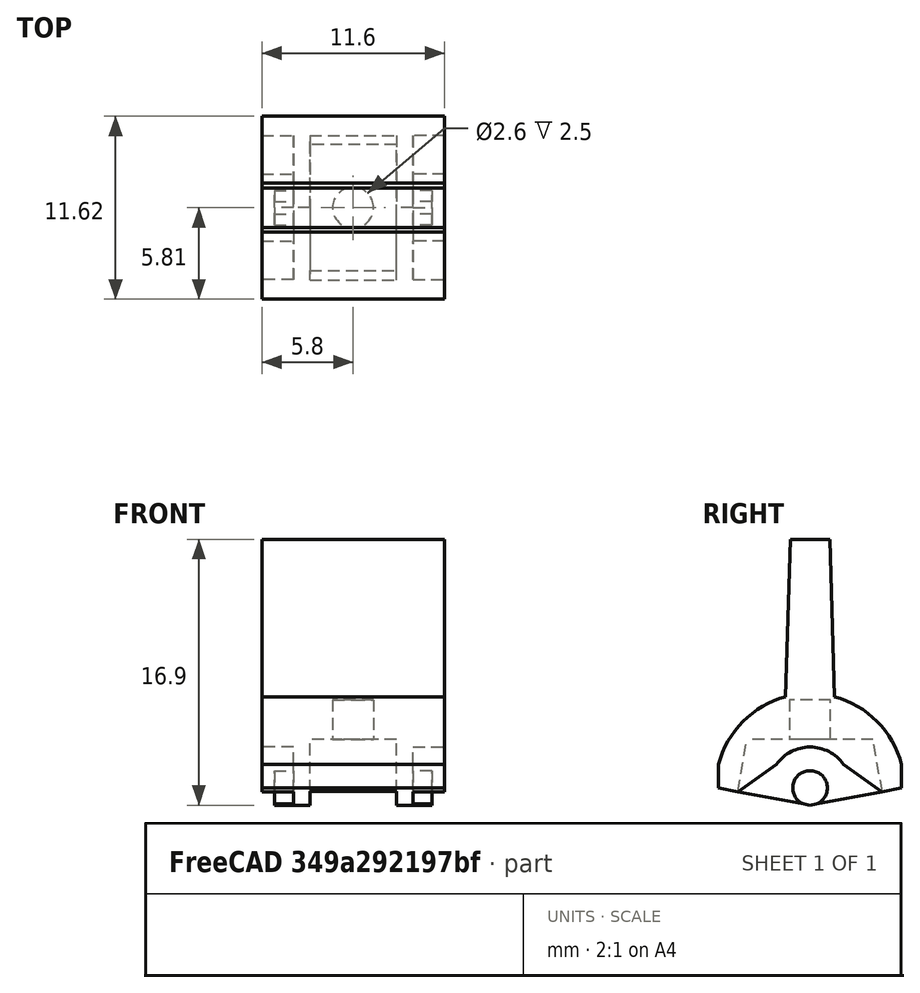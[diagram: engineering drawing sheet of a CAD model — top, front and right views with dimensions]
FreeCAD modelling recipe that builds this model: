
FCSTD DOCUMENT  (FreeCAD 1.0R39109 (Git))
Label: switch lever MA
License: All rights reserved
LicenseURL: http://en.wikipedia.org/wiki/All_rights_reserved
objects: Sketcher::SketchObject×6, PartDesign::Pocket×4, PartDesign::Pad×2, PartDesign::Mirrored×2, PartDesign::Draft×1, PartDesign::Body×1, Mesh::Feature×1
note: 38 computed .brp shape members not serialized (recipe doc carries the construction recipe); baked Part::Feature solids carry a one-line shape summary decoded from their .brp

FEATURE [Sketcher::SketchObject] Sketch
  ArcFitTolerance = 0
  AttachmentSupport = -> [XY_Plane]
  FullyConstrained = true
  MakeInternals = false
  MapMode = 5
  sketch-geometry (8):
    g0: LineSegment StartX=-15.7963 StartY=1.25 StartZ=0 EndX=-15.7963 EndY=-1.25 EndZ=0
    g1: LineSegment StartX=-15.7963 StartY=-1.25 StartZ=0 EndX=-5.79634 EndY=-1.55 EndZ=0
    g2: LineSegment StartX=-15.7963 StartY=1.25 StartZ=0 EndX=-5.79634 EndY=1.55 EndZ=0
    g3: ArcOfCircle CenterX=0 CenterY=0 CenterZ=0 NormalX=0 NormalY=0 NormalZ=1 AngleXU=0 Radius=6 StartAngle=1.82348 EndAngle=2.8803
    g4: ArcOfCircle CenterX=0 CenterY=0 CenterZ=0 NormalX=0 NormalY=0 NormalZ=1 AngleXU=0 Radius=6 StartAngle=3.40289 EndAngle=4.45971
    g5: LineSegment StartX=-1.5 StartY=5.80948 StartZ=0 EndX=1.1 EndY=5.80948 EndZ=0
    g6: LineSegment StartX=1.1 StartY=5.80948 StartZ=0 EndX=1.1 EndY=-5.80948 EndZ=0
    g7: LineSegment StartX=1.1 StartY=-5.80948 StartZ=0 EndX=-1.5 EndY=-5.80948 EndZ=0
  constraints (22):
    c: Coincident(g0,g1)
    c: Coincident(g0,g2)
    c: Coincident(g3,g-1)
    c: Coincident(g3,g2)
    c: Coincident(g4,g3)
    c: Coincident(g4,g1)
    c: Symmetric(g2,g1,g-1)
    c: Symmetric(g0,g0,g-1)
    c: Radius(g3) = 6
    c: Coincident(g5,g6)
    c: Vertical(g6)
    c: Coincident(g6,g7)
    c: Coincident(g7,g4)
    c: Horizontal(g5)
    c: Horizontal(g7)
    c: Coincident(g5,g3)
    c: Vertical(g4,g3)
    c: DistanceX(g3,g-1) = 1.5
    c: DistanceX(g5,g5) = 2.6
    c: DistanceX(g2,g2) = 10
    c: DistanceY(g1,g2) = 3.1
    c: DistanceY(g0,g0) = 2.5
FEATURE [PartDesign::Pad] Pad
  Direction = (0,0,1)
  Length = 11.6
  Length2 = 10
  Midplane = true
  Profile = -> Sketch
  ReferenceAxis = -> Sketch [N_Axis]
  Suppressed = false
  Type = 0
FEATURE [Sketcher::SketchObject] Sketch001
  ArcFitTolerance = 0
  AttachmentSupport = -> [Pad]
  ExternalGeometry = -> [Pad]
  FullyConstrained = false
  MakeInternals = false
  MapMode = 5
  Placement = pos=(0,0,5.8) rot=(0,0,1;0rad)
  sketch-geometry (4):
    g0: ArcOfCircle CenterX=-4e-16 CenterY=-3e-16 CenterZ=0 NormalX=0 NormalY=0 NormalZ=1 AngleXU=0 Radius=2.6 StartAngle=2.18575 EndAngle=4.09743
    g1: LineSegment StartX=1.1 StartY=-5.80948 StartZ=0 EndX=-1.5 EndY=-2.12368 EndZ=0
    g2: LineSegment StartX=1.1 StartY=-5.80948 StartZ=0 EndX=1.1 EndY=5.80948 EndZ=0
    g3: LineSegment StartX=1.1 StartY=5.80948 StartZ=0 EndX=-1.5 EndY=2.12368 EndZ=0
  constraints (9):
    c: DistanceX(g0,g-3) = 2.6
    c: Vertical(g0,g0)
    c: Radius(g0) = 2.6
    c: Coincident(g2,g-4)
    c: Coincident(g3,g0)
    c: Coincident(g1,g0)
    c: Coincident(g1,g2)
    c: Coincident(g1,g-5)
    c: Coincident(g3,g2)
FEATURE [PartDesign::Pocket] Pocket  label="Side pocket"
  BaseFeature = -> Pad
  Direction = (0,0,-1)
  Length = 2
  Length2 = 5
  Profile = -> Sketch001
  ReferenceAxis = -> Sketch001 [N_Axis]
  Suppressed = false
  Type = 0
FEATURE [PartDesign::Mirrored] Mirrored
  BaseFeature = -> Pocket
  MirrorPlane = -> XY_Plane
  Originals = -> [Pocket]
  Suppressed = false
  TransformMode = 0
FEATURE [Sketcher::SketchObject] Sketch002
  ArcFitTolerance = 0
  AttachmentSupport = -> [Mirrored]
  FullyConstrained = true
  MakeInternals = false
  MapMode = 5
  Placement = pos=(0,0,-3.8) rot=(1,0,0;3.14159rad)
  sketch-geometry (1):
    g0: Circle CenterX=0 CenterY=0 CenterZ=0 NormalX=0 NormalY=0 NormalZ=1 AngleXU=0 Radius=1.1
  constraints (2):
    c: Coincident(g0,g-1)
    c: Diameter(g0) = 2.2
FEATURE [PartDesign::Pad] Pad001  label="pins"
  BaseFeature = -> Mirrored
  Direction = (0,0,-1)
  Length = 1.2
  Length2 = 10
  Profile = -> Sketch002
  ReferenceAxis = -> Sketch002 [N_Axis]
  Suppressed = false
  Type = 0
FEATURE [PartDesign::Mirrored] Mirrored001  label="Mirrored pins"
  BaseFeature = -> Pad001
  MirrorPlane = -> XY_Plane
  Originals = -> [Pad001]
  Suppressed = false
  TransformMode = 0
FEATURE [Sketcher::SketchObject] Sketch003
  ArcFitTolerance = 0
  AttachmentSupport = -> [Mirrored001]
  FullyConstrained = true
  MakeInternals = false
  MapMode = 5
  Placement = pos=(1.1,0,0) rot=(0.57735,0.57735,0.57735;2.0944rad)
  sketch-geometry (4):
    g0: LineSegment StartX=-4 StartY=2.75 StartZ=0 EndX=4 EndY=2.75 EndZ=0
    g1: LineSegment StartX=4 StartY=2.75 StartZ=0 EndX=4 EndY=-2.75 EndZ=0
    g2: LineSegment StartX=4 StartY=-2.75 StartZ=0 EndX=-4 EndY=-2.75 EndZ=0
    g3: LineSegment StartX=-4 StartY=-2.75 StartZ=0 EndX=-4 EndY=2.75 EndZ=0
  constraints (11):
    c: Coincident(g0,g1)
    c: Coincident(g1,g2)
    c: Coincident(g2,g3)
    c: Coincident(g3,g0)
    c: Horizontal(g0)
    c: Horizontal(g2)
    c: Vertical(g1)
    c: Vertical(g3)
    c: Symmetric(g0,g1,g-1)
    c: DistanceX(g0,g0) = 8
    c: DistanceY(g3,g3) = 5.5
FEATURE [PartDesign::Pocket] Pocket001  label="bottom square pocket"
  BaseFeature = -> Mirrored001
  Direction = (-1,0,0)
  Length = 4.2
  Length2 = 5
  Profile = -> Sketch003
  ReferenceAxis = -> Sketch003 [N_Axis]
  Suppressed = false
  Type = 0
FEATURE [Sketcher::SketchObject] Sketch004
  ArcFitTolerance = 0
  AttachmentSupport = -> [Pocket001]
  FullyConstrained = true
  MakeInternals = false
  MapMode = 5
  Placement = pos=(-3.1,0,0) rot=(0.57735,0.57735,0.57735;2.0944rad)
  sketch-geometry (1):
    g0: Circle CenterX=0 CenterY=0 CenterZ=0 NormalX=0 NormalY=0 NormalZ=1 AngleXU=0 Radius=1.3
  constraints (2):
    c: Coincident(g0,g-1)
    c: Diameter(g0) = 2.6
FEATURE [PartDesign::Pocket] Pocket002  label="lever pin pocket"
  BaseFeature = -> Pocket001
  Direction = (-1,0,0)
  Length = 2.5
  Length2 = 5
  Profile = -> Sketch004
  ReferenceAxis = -> Sketch004 [N_Axis]
  Suppressed = false
  Type = 0
FEATURE [Sketcher::SketchObject] Sketch005
  ArcFitTolerance = 0
  AttachmentSupport = -> [Pocket002]
  ExternalGeometry = -> [Pocket002]
  FullyConstrained = false
  MakeInternals = false
  MapMode = 5
  Placement = pos=(0,0,5.8) rot=(0,0,1;0rad)
  sketch-geometry (5):
    g0: LineSegment StartX=1.1 StartY=0 StartZ=0 EndX=0 EndY=-5.80948 EndZ=0
    g1: LineSegment StartX=1.1 StartY=0 StartZ=0 EndX=0 EndY=5.80948 EndZ=0
    g2: LineSegment StartX=0 StartY=5.80948 StartZ=0 EndX=1.32725 EndY=5.80948 EndZ=0
    g3: LineSegment StartX=1.32725 StartY=5.80948 StartZ=0 EndX=1.32725 EndY=-5.80948 EndZ=0
    g4: LineSegment StartX=0 StartY=-5.80948 StartZ=0 EndX=1.32725 EndY=-5.80948 EndZ=0
  constraints (14):
    c: PointOnObject(g0,g-1)
    c: PointOnObject(g0,g-4)
    c: Coincident(g1,g0)
    c: PointOnObject(g1,g-3)
    c: Coincident(g2,g1)
    c: Horizontal(g2)
    c: Coincident(g3,g2)
    c: Vertical(g3)
    c: Coincident(g4,g0)
    c: Coincident(g4,g3)
    c: PointOnObject(g-4,g4)
    c: PointOnObject(g0,g-2)
    c: PointOnObject(g1,g-2)
    c: PointOnObject(g0,g-5)
FEATURE [PartDesign::Pocket] Pocket003
  BaseFeature = -> Pocket002
  Direction = (0,0,-1)
  Length = 5
  Length2 = 5
  Profile = -> Sketch005
  ReferenceAxis = -> Sketch005 [N_Axis]
  Suppressed = false
  Type = 1
FEATURE [PartDesign::Draft] Draft
  Angle = 10
  Base = -> Pocket003 [Face27,Face25]
  BaseFeature = -> Pocket003
  NeutralPlane = -> Pocket003 [Face28]
  Refine = true
  SupportTransform = false
  Suppressed = false
FEATURE [PartDesign::Body] Body
  AllowCompound = false
  Group = -> [Sketch,Pad,Sketch001,Pocket,Mirrored,Sketch002,Pad001,Mirrored001,Sketch003,Pocket001,Sketch004,Pocket002,Sketch005,Pocket003,Draft]
  Origin = -> Origin
  Placement = pos=(0,0,0) rot=(0,1,0;1.5708rad)
  Tip = -> Draft
FEATURE [Mesh::Feature] Mesh  label="Body (Meshed)"
